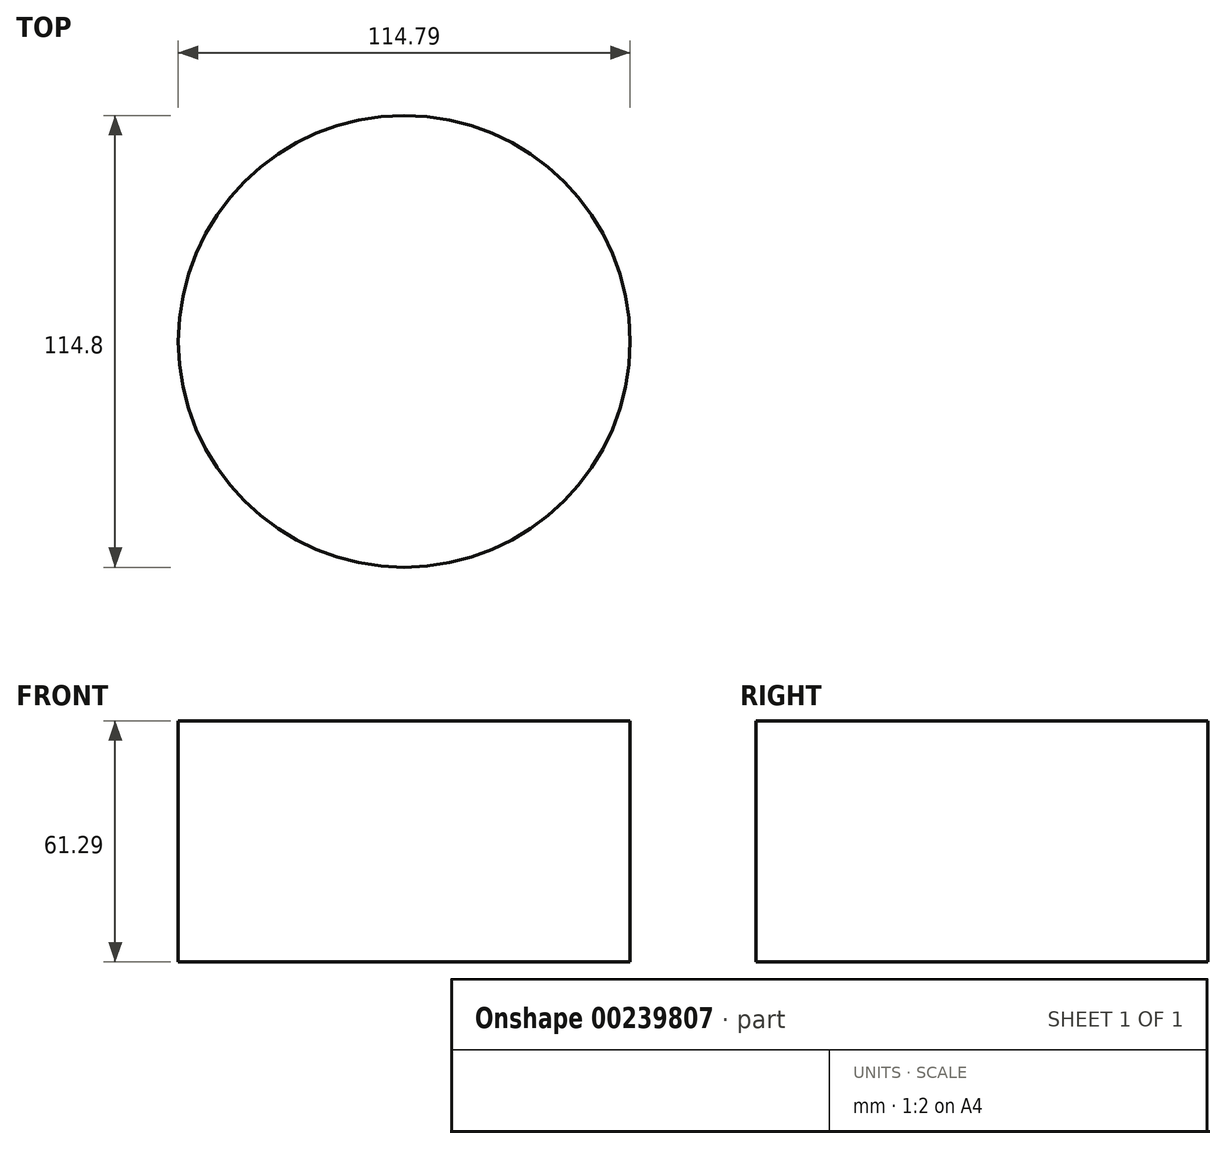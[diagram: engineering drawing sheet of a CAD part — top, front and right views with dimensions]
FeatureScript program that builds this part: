
annotation { "Feature Type Name" : "Feature", "Feature Type Description" : "" }
export const myFeature = defineFeature(function(context is Context, id is Id, definition is map)
    precondition{}
    {
        {
            var Q0;
            Q0=qCreatedBy(makeId("Front.planeOp"),FACE);
            var sketch = newSketch(context, id + "F0", { "sketchPlane" : qUnion([Q0])});
            skLineSegment(sketch, "E0.bottom", {"start": v(-57.4, 61.3) * mm, "end": v(0, 61.3) * mm});
            skLineSegment(sketch, "E0.top", {"start": v(-57.4, 0) * mm, "end": v(0, 0) * mm});
            skLineSegment(sketch, "E0.left", {"start": v(-57.4, 61.3) * mm, "end": v(-57.4, 0) * mm});
            skLineSegment(sketch, "E0.right", {"start": v(0, 61.3) * mm, "end": v(0, 0) * mm});
            skSolve(sketch);
        }
        {
            var Q0;
            Q0 = qSketchRegion(id + "F0", true);
            var Q1;
            Q1=sQuery(id+"F0.wireOp",EDGE,"E0.left");
            revolve(context, id + "F1", {"entities" : qUnion([Q0]), "axis" : qUnion([Q1]), "revolveType" : RevolveType.FULL});
        }
    });
